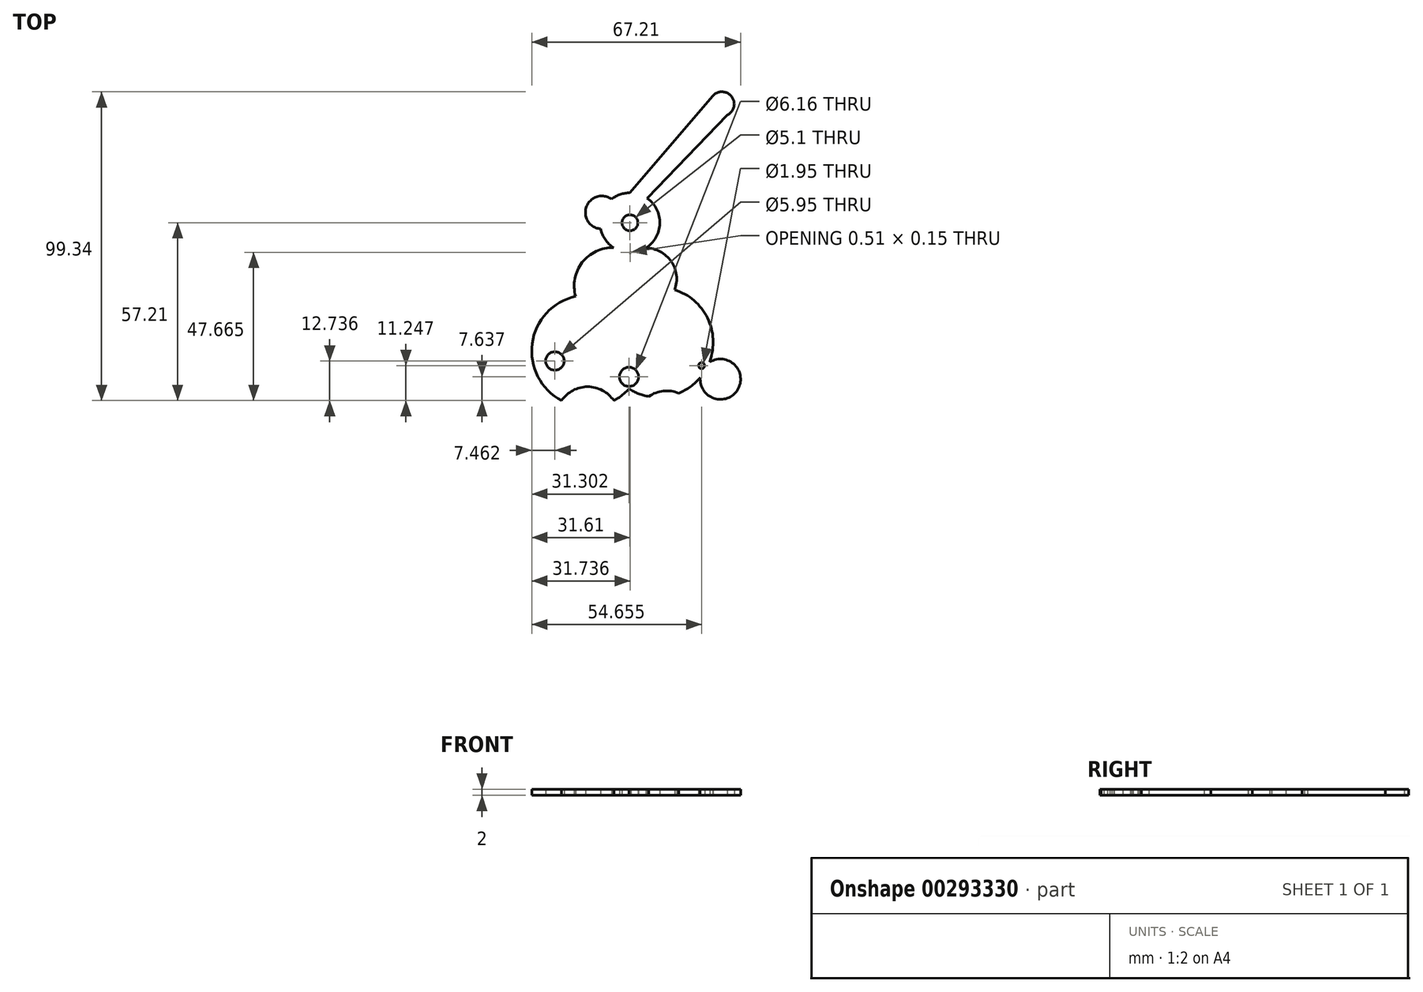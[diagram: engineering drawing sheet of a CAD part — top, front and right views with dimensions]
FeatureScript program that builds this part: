
annotation { "Feature Type Name" : "Feature", "Feature Type Description" : "" }
export const myFeature = defineFeature(function(context is Context, id is Id, definition is map)
    precondition{}
    {
        {
            var Q0;
            Q0=qCreatedBy(makeId("Top.planeOp"),FACE);
            var sketch = newSketch(context, id + "F0", { "sketchPlane" : qUnion([Q0])});
            skCircle(sketch, "E0", {"center": v(0, 0) * mm, "radius": 2.55 * mm});
            skArc(sketch, "E1", {"start": v(-0.13, -9.62) * mm, "mid": v(0.13, -9.62) * mm, "end": v(0.38, -9.61) * mm});
            skArc(sketch, "E2", {"start": v(-5.91, 7.6) * mm, "mid": v(-14.01, 5.13) * mm, "end": v(-9.41, -1.98) * mm});
            skCircle(sketch, "E3", {"center": v(29.6, 38.19) * mm, "radius": 3.94 * mm});
            skLineSegment(sketch, "E4", {"start": v(26.63, 40.8) * mm, "end": v(0, 9.62) * mm});
            skLineSegment(sketch, "E5", {"start": v(33.2, 36.6) * mm, "end": v(5.57, 7.84) * mm});
            skArc(sketch, "E6", {"start": v(14.37, -21.56) * mm, "mid": v(13.27, -12.43) * mm, "end": v(5.15, -8.13) * mm});
            skArc(sketch, "E7", {"start": v(0.38, -9.61) * mm, "mid": v(0.25, -9.54) * mm, "end": v(0.12, -9.47) * mm});
            skArc(sketch, "E8", {"start": v(-17.48, -23.68) * mm, "mid": v(-31.45, -38.87) * mm, "end": v(-22, -57.21) * mm});
            skArc(sketch, "E9", {"start": v(-0.3, -53.45) * mm, "mid": v(2.77, -54.98) * mm, "end": v(6.1, -55.88) * mm});
            skArc(sketch, "E10", {"start": v(22.63, -49.8) * mm, "mid": v(34.69, -53.65) * mm, "end": v(25.54, -44.9) * mm});
            skArc(sketch, "E11.trimOffspring", {"start": v(-2.18, -24.78) * mm, "mid": v(-2.97, -25.47) * mm, "end": v(-3.71, -26.2) * mm});
            skArc(sketch, "E12.trimOffspring", {"start": v(25.54, -44.9) * mm, "mid": v(25.03, -30.8) * mm, "end": v(14.37, -21.56) * mm});
            skArc(sketch, "E13.trimOffspring", {"start": v(5.15, -8.13) * mm, "mid": v(9.62, -0.26) * mm, "end": v(5.57, 7.84) * mm});
            skArc(sketch, "E14.trimOffspring", {"start": v(0.12, -9.47) * mm, "mid": v(0, -9.54) * mm, "end": v(-0.13, -9.62) * mm});
            skArc(sketch, "E15.trimOffspring", {"start": v(-5.3, -8.03) * mm, "mid": v(-15.36, -12.76) * mm, "end": v(-17.48, -23.68) * mm});
            skArc(sketch, "E16.trimOffspring", {"start": v(0, 9.62) * mm, "mid": v(-3.12, 9.1) * mm, "end": v(-5.91, 7.6) * mm});
            skArc(sketch, "E17.trimOffspring", {"start": v(-9.41, -1.98) * mm, "mid": v(-7.95, -5.41) * mm, "end": v(-5.3, -8.03) * mm});
            skArc(sketch, "E18", {"start": v(-5.2, -57.21) * mm, "mid": v(-13.6, -52.75) * mm, "end": v(-22, -57.21) * mm});
            skArc(sketch, "E19", {"start": v(15.7, -54.85) * mm, "mid": v(10.76, -54.12) * mm, "end": v(6.1, -55.88) * mm});
            skCircle(sketch, "E20", {"center": v(-0.3, -49.57) * mm, "radius": 3.08 * mm});
            skArc(sketch, "E21.trimOffspring", {"start": v(-5.2, -57.21) * mm, "mid": v(-2.59, -55.54) * mm, "end": v(-0.3, -53.45) * mm});
            skArc(sketch, "E22.trimOffspring", {"start": v(15.7, -54.85) * mm, "mid": v(19.47, -52.75) * mm, "end": v(22.63, -49.8) * mm});
            skCircle(sketch, "E23", {"center": v(-24.15, -44.47) * mm, "radius": 0.97 * mm});
            skCircle(sketch, "E24", {"center": v(23.05, -45.96) * mm, "radius": 0.98 * mm});
            skCircle(sketch, "E25", {"center": v(-24.15, -44.47) * mm, "radius": 2.98 * mm});
            skCircle(sketch, "E26", {"center": v(23.05, -45.96) * mm, "radius": 2.98 * mm});
            skSolve(sketch);
        }
        {
            var Q0;
            Q0 = qSketchRegion(id + "F0", true);
            extrude(context, id + "F1", {"entities" : qUnion([Q0]), "depth" : 2 * mm});
        }
    });
